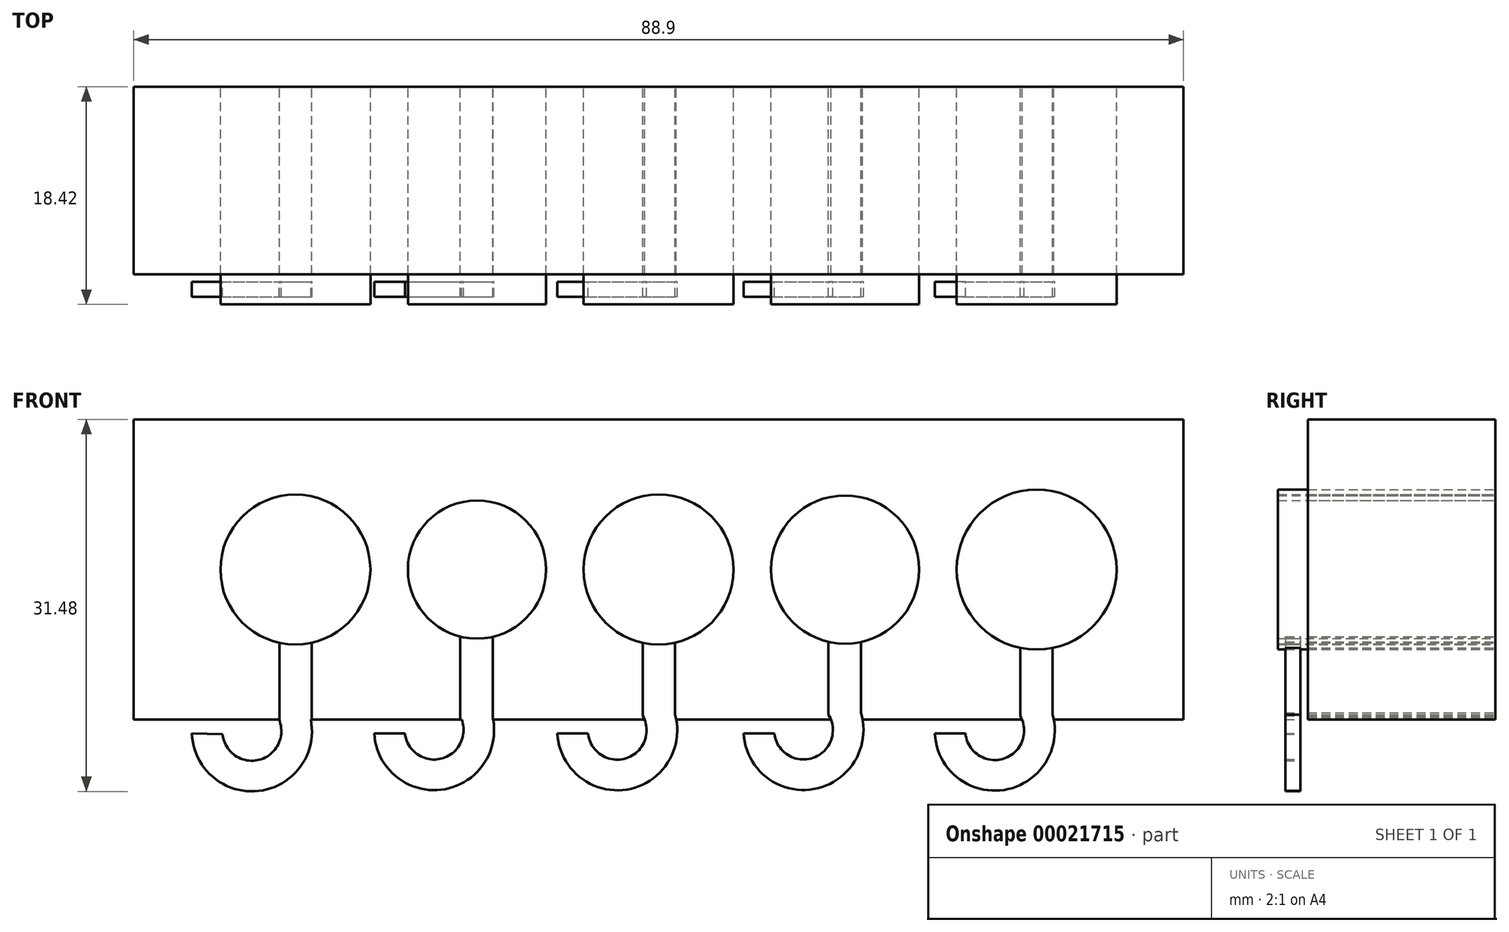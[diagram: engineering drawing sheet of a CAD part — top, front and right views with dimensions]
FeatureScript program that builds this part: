
annotation { "Feature Type Name" : "Feature", "Feature Type Description" : "" }
export const myFeature = defineFeature(function(context is Context, id is Id, definition is map)
    precondition{}
    {
        {
            var Q0;
            Q0=qCreatedBy(makeId("Front.planeOp"),FACE);
            var sketch = newSketch(context, id + "F0", { "sketchPlane" : qUnion([Q0])});
            skLineSegment(sketch, "E0.rect.bottom", {"start": v(44.45, 12.7) * mm, "end": v(-44.45, 12.7) * mm});
            skLineSegment(sketch, "E0.rect.top", {"start": v(44.45, -12.7) * mm, "end": v(-29.45, -12.7) * mm});
            skLineSegment(sketch, "E0.rect.left", {"start": v(44.45, 12.7) * mm, "end": v(44.45, -12.7) * mm});
            skLineSegment(sketch, "E0.rect.right", {"start": v(-44.45, 12.7) * mm, "end": v(-44.45, -12.7) * mm});
            skPoint(sketch, "E0.rect.middle", {"position": v(0, 0) * mm});
            skCircle(sketch, "E1", {"center": v(-30.76, 0) * mm, "radius": 6.35 * mm});
            skLineSegment(sketch, "E2", {"start": v(-37.1, 0) * mm, "end": v(-37.1, 36.8) * mm, "construction": true});
            skLineSegment(sketch, "E3", {"start": v(-43.46, 17.73) * mm, "end": v(-37.1, 17.73) * mm});
            skCircle(sketch, "E4", {"center": v(32.01, 0) * mm, "radius": 6.77 * mm});
            skLineSegment(sketch, "E5", {"start": v(38.78, 0) * mm, "end": v(38.78, 31.95) * mm, "construction": true});
            skLineSegment(sketch, "E6", {"start": v(45.13, 21.15) * mm, "end": v(38.78, 21.15) * mm});
            skLineSegment(sketch, "E7", {"start": v(-24.4, 0) * mm, "end": v(-24.4, 34.47) * mm, "construction": true});
            skLineSegment(sketch, "E8", {"start": v(25.24, 0) * mm, "end": v(25.24, 37.53) * mm, "construction": true});
            skCircle(sketch, "E9", {"center": v(-15.38, 0) * mm, "radius": 5.85 * mm});
            skCircle(sketch, "E10", {"center": v(15.8, 0) * mm, "radius": 6.27 * mm});
            skCircle(sketch, "E11", {"center": v(0, 0) * mm, "radius": 6.35 * mm});
            skLineSegment(sketch, "E12", {"start": v(-21.23, 0) * mm, "end": v(-21.23, 38.25) * mm, "construction": true});
            skLineSegment(sketch, "E13", {"start": v(22.07, 0) * mm, "end": v(22.07, 46) * mm, "construction": true});
            skLineSegment(sketch, "E14", {"start": v(6.35, 0) * mm, "end": v(6.35, 46.17) * mm, "construction": true});
            skLineSegment(sketch, "E15", {"start": v(9.53, 0) * mm, "end": v(9.53, 46.9) * mm, "construction": true});
            skLineSegment(sketch, "E16", {"start": v(-9.52, 0) * mm, "end": v(-9.53, 44.37) * mm, "construction": true});
            skLineSegment(sketch, "E17", {"start": v(-6.35, 0) * mm, "end": v(-6.35, 44.73) * mm, "construction": true});
            skLineSegment(sketch, "E18", {"start": v(-24.4, 28.71) * mm, "end": v(-21.23, 28.71) * mm});
            skLineSegment(sketch, "E19", {"start": v(-9.53, 28.9) * mm, "end": v(-6.35, 28.9) * mm});
            skLineSegment(sketch, "E20", {"start": v(6.35, 28.53) * mm, "end": v(9.53, 28.53) * mm});
            skLineSegment(sketch, "E21", {"start": v(22.07, 31.23) * mm, "end": v(25.24, 31.23) * mm});
            skLineSegment(sketch, "E22", {"start": v(-30.76, -10.16) * mm, "end": v(51.15, -10.16) * mm, "construction": true});
            skLineSegment(sketch, "E23", {"start": v(-32.11, 0) * mm, "end": v(-29.36, 0) * mm});
            skLineSegment(sketch, "E24", {"start": v(-29.36, 0) * mm, "end": v(-29.36, -12.7) * mm});
            skLineSegment(sketch, "E25", {"start": v(-32.11, 0) * mm, "end": v(-32.11, -12.7) * mm});
            skArc(sketch, "E26", {"start": v(-39.53, -13.86) * mm, "mid": v(-33.86, -18.74) * mm, "end": v(-29.45, -12.7) * mm});
            skArc(sketch, "E27", {"start": v(-36.93, -13.94) * mm, "mid": v(-33.81, -16.1) * mm, "end": v(-32.15, -12.7) * mm});
            skLineSegment(sketch, "E28", {"start": v(-36.93, -13.94) * mm, "end": v(-39.53, -13.86) * mm});
            skLineSegment(sketch, "E29.trimOffspring", {"start": v(-32.11, -12.7) * mm, "end": v(-44.45, -12.7) * mm});
            skLineSegment(sketch, "E30", {"start": v(-16.8, 0) * mm, "end": v(-14.05, 0) * mm});
            skLineSegment(sketch, "E31", {"start": v(-16.8, 0) * mm, "end": v(-16.8, -12.7) * mm});
            skLineSegment(sketch, "E32", {"start": v(-14.05, 0) * mm, "end": v(-14.05, -12.7) * mm});
            skArc(sketch, "E33", {"start": v(-24.08, -13.86) * mm, "mid": v(-18.32, -18.63) * mm, "end": v(-14.05, -12.5) * mm});
            skLineSegment(sketch, "E34", {"start": v(-33.86, -18.74) * mm, "end": v(51.32, -18.74) * mm, "construction": true});
            skArc(sketch, "E35", {"start": v(-21.48, -13.86) * mm, "mid": v(-18.42, -16.01) * mm, "end": v(-16.68, -12.7) * mm});
            skLineSegment(sketch, "E36", {"start": v(-39.53, -13.86) * mm, "end": v(51.01, -13.86) * mm, "construction": true});
            skLineSegment(sketch, "E37", {"start": v(-24.08, -13.86) * mm, "end": v(-21.48, -13.86) * mm});
            skLineSegment(sketch, "E38", {"start": v(-1.34, 0) * mm, "end": v(1.4, 0) * mm});
            skLineSegment(sketch, "E39", {"start": v(-1.34, 0) * mm, "end": v(-1.34, -12.37) * mm});
            skLineSegment(sketch, "E40", {"start": v(1.4, 0) * mm, "end": v(1.4, -12.29) * mm});
            skLineSegment(sketch, "E41", {"start": v(14.4, 0) * mm, "end": v(17.14, 0) * mm});
            skLineSegment(sketch, "E42", {"start": v(30.62, 0) * mm, "end": v(33.36, 0) * mm});
            skLineSegment(sketch, "E43", {"start": v(14.4, 0) * mm, "end": v(14.4, -12.28) * mm});
            skLineSegment(sketch, "E44", {"start": v(17.14, 0) * mm, "end": v(17.14, -12.12) * mm});
            skLineSegment(sketch, "E45", {"start": v(30.62, 0) * mm, "end": v(30.62, -12.38) * mm});
            skLineSegment(sketch, "E46", {"start": v(33.36, 0) * mm, "end": v(33.36, -12.28) * mm});
            skArc(sketch, "E47", {"start": v(7.2, -13.86) * mm, "mid": v(13.15, -18.59) * mm, "end": v(17.14, -12.12) * mm});
            skArc(sketch, "E48", {"start": v(9.8, -13.86) * mm, "mid": v(13.08, -15.94) * mm, "end": v(14.4, -12.28) * mm});
            skLineSegment(sketch, "E49", {"start": v(7.2, -13.86) * mm, "end": v(9.8, -13.86) * mm});
            skArc(sketch, "E50", {"start": v(-8.58, -13.86) * mm, "mid": v(-2.71, -18.62) * mm, "end": v(1.4, -12.29) * mm});
            skArc(sketch, "E51", {"start": v(-5.98, -13.86) * mm, "mid": v(-2.74, -15.97) * mm, "end": v(-1.34, -12.37) * mm});
            skLineSegment(sketch, "E52", {"start": v(-8.58, -13.86) * mm, "end": v(-5.98, -13.86) * mm});
            skArc(sketch, "E53", {"start": v(23.4, -13.86) * mm, "mid": v(29.27, -18.65) * mm, "end": v(33.36, -12.28) * mm});
            skArc(sketch, "E54", {"start": v(25.99, -13.86) * mm, "mid": v(29.23, -16) * mm, "end": v(30.62, -12.38) * mm});
            skLineSegment(sketch, "E55", {"start": v(25.99, -13.86) * mm, "end": v(23.4, -13.86) * mm});
            skSolve(sketch);
        }
        {
            var Q0;
            Q0=makeQuery(id+"F0.imprint","IMPRINT",FACE,{"disambiguationData":[TD([[makeQuery(id+"F0.imprint","IMPRINT",EDGE,{"derivedFrom":sQuery(id+"F0.wireOp",EDGE,"E9")}),1.0]])]});
            var Q1;
            Q1=makeQuery(id+"F0.imprint","IMPRINT",FACE,{"disambiguationData":[TD([[makeQuery(id+"F0.imprint","IMPRINT",EDGE,{"derivedFrom":sQuery(id+"F0.wireOp",EDGE,"E1")}),1.0]])]});
            var Q2;
            Q2=makeQuery(id+"F0.imprint","IMPRINT",FACE,{"disambiguationData":[TD([[makeQuery(id+"F0.imprint","IMPRINT",EDGE,{"derivedFrom":sQuery(id+"F0.wireOp",EDGE,"E11")}),1.0]])]});
            var Q3;
            Q3=makeQuery(id+"F0.imprint","IMPRINT",FACE,{"disambiguationData":[TD([[makeQuery(id+"F0.imprint","IMPRINT",EDGE,{"derivedFrom":sQuery(id+"F0.wireOp",EDGE,"E10")}),1.0]])]});
            var Q4;
            Q4=makeQuery(id+"F0.imprint","IMPRINT",FACE,{"disambiguationData":[TD([[makeQuery(id+"F0.imprint","IMPRINT",EDGE,{"derivedFrom":sQuery(id+"F0.wireOp",EDGE,"E4")}),1.0]])]});
            extrude(context, id + "F1", {"entities" : qUnion([Q0, Q1, Q2, Q3, Q4]), "depth" : 18.41 * mm});
        }
        {
            var Q0;
            Q0=makeQuery(id+"F0.imprint","IMPRINT",FACE,{"disambiguationData":[TD([[makeQuery(id+"F0.imprint","IMPRINT",EDGE,{"derivedFrom":sQuery(id+"F0.wireOp",EDGE,"E0.rect.bottom")}),1.0]])]});
            extrude(context, id + "F2", {"entities" : qUnion([Q0]), "depth" : 15.88 * mm});
        }
        {
            var Q0;
            {var subQ0=sQuery(id+"F0.wireOp",EDGE,"b70a9239-2a18-4bbb-92f1-a8609fe238bc");Q0=makeQuery(id+"F0.imprint","IMPRINT",FACE,{"disambiguationData":[TD([[makeQuery(id+"F0.imprint","IMPRINT",EDGE,{"derivedFrom":subQ0}),1.0]])]});}
            var Q1;
            {var subQ1=sQuery(id+"F0.wireOp",EDGE,"E1");var subQ5=sQuery(id+"F0.wireOp",EDGE,"df3efdb1-77fe-4e60-8634-914056b6db91");var subQ6=makeQuery(id+"F0.imprint","INTERSECT",VERTEX,{"derivedFrom":[subQ1,subQ5]});Q1=makeQuery(id+"F0.imprint","IMPRINT",FACE,{"disambiguationData":[TD([[makeQuery(id+"F0.imprint","IMPRINT",EDGE,{"disambiguationData":[TD([[subQ6,-1.0]])],"derivedFrom":subQ1}),-1.0]])]});}
            var Q2;
            {var subQ1=sQuery(id+"F0.wireOp",EDGE,"9934a529-79d0-48cc-adc5-041acf62495c");Q2=makeQuery(id+"F0.imprint","IMPRINT",FACE,{"disambiguationData":[TD([[makeQuery(id+"F0.imprint","IMPRINT",EDGE,{"derivedFrom":subQ1}),1.0]])]});}
            var Q3;
            {var subQ1=sQuery(id+"F0.wireOp",EDGE,"E35");Q3=makeQuery(id+"F0.imprint","IMPRINT",FACE,{"disambiguationData":[TD([[makeQuery(id+"F0.imprint","IMPRINT",EDGE,{"derivedFrom":subQ1}),-1.0]])]});}
            var Q4;
            {var subQ0=sQuery(id+"F0.wireOp",EDGE,"E32");var subQ2=sQuery(id+"F0.wireOp",EDGE,"E0.rect.top");var subQ3=makeQuery(id+"F0.imprint","INTERSECT",VERTEX,{"derivedFrom":[subQ2,subQ0]});Q4=makeQuery(id+"F0.imprint","IMPRINT",FACE,{"disambiguationData":[TD([[makeQuery(id+"F0.imprint","IMPRINT",EDGE,{"disambiguationData":[TD([[subQ3,-1.0]])],"derivedFrom":subQ2}),-1.0]])]});}
            var Q5;
            {var subQ0=sQuery(id+"F0.wireOp",EDGE,"E52");Q5=makeQuery(id+"F0.imprint","IMPRINT",FACE,{"disambiguationData":[TD([[makeQuery(id+"F0.imprint","IMPRINT",EDGE,{"derivedFrom":subQ0}),-1.0]])]});}
            var Q6;
            {var subQ0=sQuery(id+"F0.wireOp",EDGE,"E49");Q6=makeQuery(id+"F0.imprint","IMPRINT",FACE,{"disambiguationData":[TD([[makeQuery(id+"F0.imprint","IMPRINT",EDGE,{"derivedFrom":subQ0}),-1.0]])]});}
            var Q7;
            {var subQ0=sQuery(id+"F0.wireOp",EDGE,"E55");Q7=makeQuery(id+"F0.imprint","IMPRINT",FACE,{"disambiguationData":[TD([[makeQuery(id+"F0.imprint","IMPRINT",EDGE,{"derivedFrom":subQ0}),1.0]])]});}
            var Q8;
            {var subQ1=sQuery(id+"F0.wireOp",EDGE,"E0.rect.top");var subQ5=sQuery(id+"F0.wireOp",EDGE,"E53");var subQ6=makeQuery(id+"F0.imprint","INTERSECT",VERTEX,{"derivedFrom":[subQ1,subQ5]});Q8=makeQuery(id+"F0.imprint","IMPRINT",FACE,{"disambiguationData":[TD([[makeQuery(id+"F0.imprint","IMPRINT",EDGE,{"disambiguationData":[TD([[subQ6,-1.0]])],"derivedFrom":subQ1}),-1.0]])]});}
            var Q9;
            {var subQ1=sQuery(id+"F0.wireOp",EDGE,"E0.rect.top");var subQ5=sQuery(id+"F0.wireOp",EDGE,"E47");var subQ6=makeQuery(id+"F0.imprint","INTERSECT",VERTEX,{"derivedFrom":[subQ1,subQ5]});Q9=makeQuery(id+"F0.imprint","IMPRINT",FACE,{"disambiguationData":[TD([[makeQuery(id+"F0.imprint","IMPRINT",EDGE,{"disambiguationData":[TD([[subQ6,-1.0]])],"derivedFrom":subQ1}),-1.0]])]});}
            var Q10;
            {var subQ1=sQuery(id+"F0.wireOp",EDGE,"E0.rect.top");var subQ5=sQuery(id+"F0.wireOp",EDGE,"E50");var subQ6=makeQuery(id+"F0.imprint","INTERSECT",VERTEX,{"derivedFrom":[subQ1,subQ5]});Q10=makeQuery(id+"F0.imprint","IMPRINT",FACE,{"disambiguationData":[TD([[makeQuery(id+"F0.imprint","IMPRINT",EDGE,{"disambiguationData":[TD([[subQ6,-1.0]])],"derivedFrom":subQ1}),-1.0]])]});}
            var Q11;
            Q11=sQuery(id+"F0.wireOp",EDGE,"E27");
            var Q12;
            Q12=sQuery(id+"F0.wireOp",EDGE,"E26");
            var Q13;
            Q13=sQuery(id+"F0.wireOp",EDGE,"E28");
            var Q14;
            Q14=sQuery(id+"F0.wireOp",EDGE,"E24");
            var Q15;
            Q15=sQuery(id+"F0.wireOp",EDGE,"E25");
            var Q16;
            Q16=sQuery(id+"F0.wireOp",EDGE,"E23");
            extrude(context, id + "F3", {"entities" : qUnion([Q0, Q1, Q2, Q3, Q4, Q5, Q6, Q7, Q8, Q9, Q10]), "surfaceEntities" : qUnion([Q11, Q12, Q13, Q14, Q15, Q16]), "depth" : 17.78 * mm, "hasSecondDirection" : true, "secondDirectionOppositeDirection" : false, "secondDirectionDepth" : 16.5 * mm});
        }
    });
